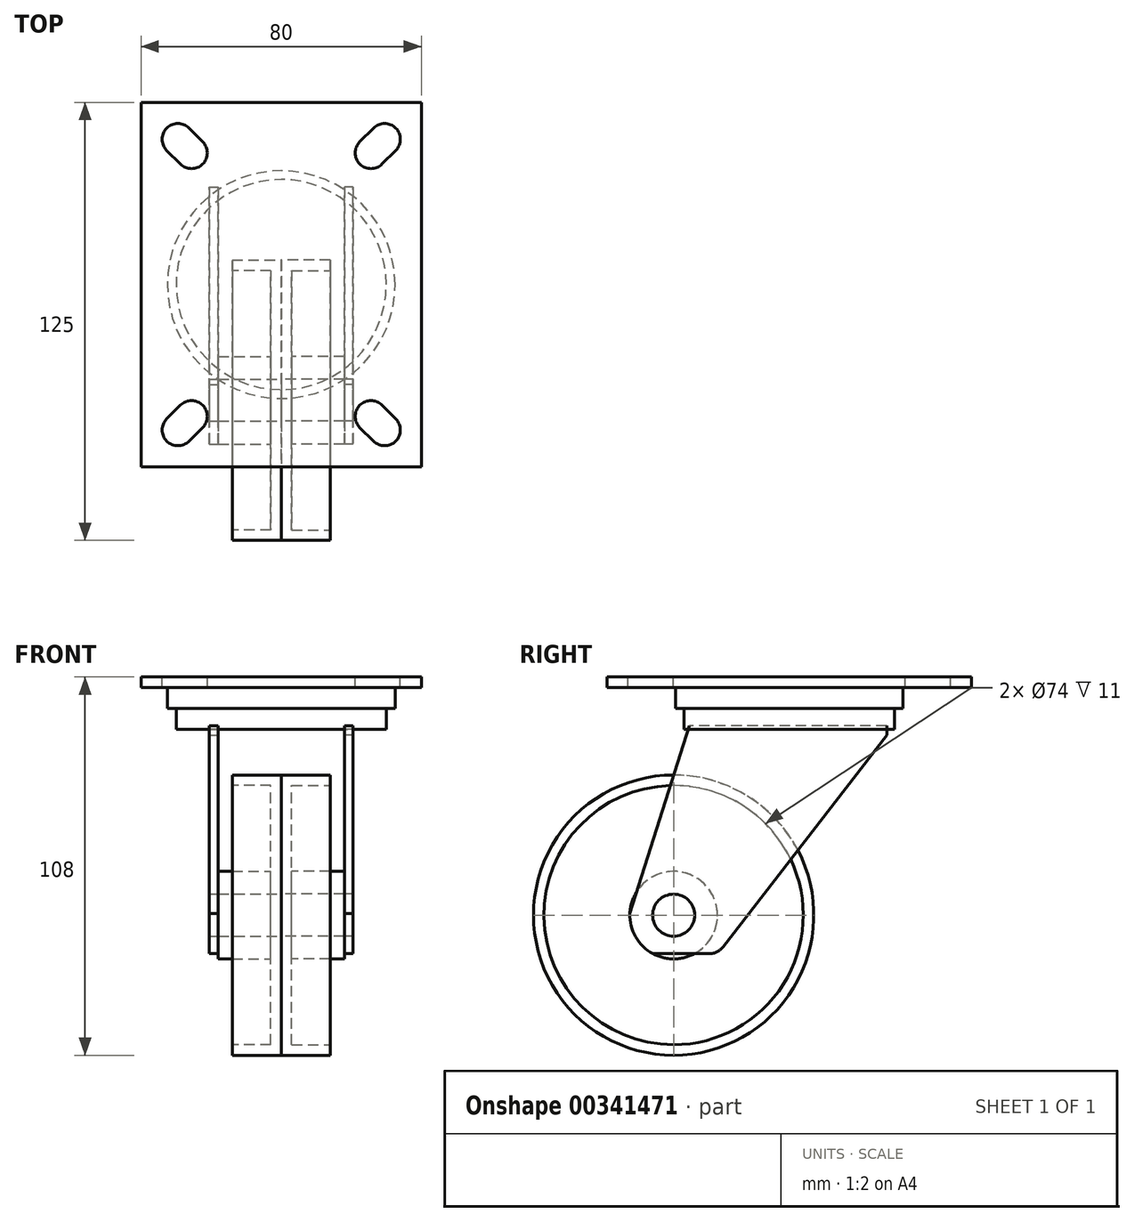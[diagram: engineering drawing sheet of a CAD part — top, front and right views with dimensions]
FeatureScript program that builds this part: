
annotation { "Feature Type Name" : "Feature", "Feature Type Description" : "" }
export const myFeature = defineFeature(function(context is Context, id is Id, definition is map)
    precondition{}
    {
        {
            var Q0;
            Q0=qCreatedBy(makeId("Front.planeOp"),FACE);
            var sketch = newSketch(context, id + "F0", { "sketchPlane" : qUnion([Q0])});
            skLineSegment(sketch, "E0.bottom", {"start": v(-49.77, 0) * mm, "end": v(53.7, 0) * mm, "construction": true});
            skLineSegment(sketch, "E0.top", {"start": v(-49.77, -108) * mm, "end": v(53.7, -108) * mm, "construction": true});
            skLineSegment(sketch, "E0.left", {"start": v(-49.77, 0) * mm, "end": v(-49.77, -108) * mm, "construction": true});
            skLineSegment(sketch, "E0.right", {"start": v(53.7, 0) * mm, "end": v(53.7, -108) * mm, "construction": true});
            skSolve(sketch);
        }
        {
            var Q0;
            Q0=qCreatedBy(makeId("Top.planeOp"),FACE);
            var sketch = newSketch(context, id + "F1", { "sketchPlane" : qUnion([Q0])});
            skLineSegment(sketch, "E1.bottom", {"start": v(-40, 52) * mm, "end": v(40, 52) * mm});
            skLineSegment(sketch, "E1.top", {"start": v(-40, -52) * mm, "end": v(40, -52) * mm});
            skLineSegment(sketch, "E1.left", {"start": v(-40, 52) * mm, "end": v(-40, -52) * mm});
            skLineSegment(sketch, "E1.right", {"start": v(40, 52) * mm, "end": v(40, -52) * mm});
            skLineSegment(sketch, "E2", {"start": v(0, 52) * mm, "end": v(0, -52) * mm, "construction": true});
            skLineSegment(sketch, "E3", {"start": v(-40, 0) * mm, "end": v(0, 0) * mm, "construction": true});
            skLineSegment(sketch, "E4", {"start": v(0, 0) * mm, "end": v(40, 0) * mm, "construction": true});
            skArc(sketch, "E5", {"start": v(-26.32, 44.68) * mm, "mid": v(-32.68, 44.68) * mm, "end": v(-32.68, 38.32) * mm});
            skLineSegment(sketch, "E6", {"start": v(-29.5, 41.5) * mm, "end": v(-26.32, 44.68) * mm, "construction": true});
            skLineSegment(sketch, "E7", {"start": v(-26.32, 44.68) * mm, "end": v(-22.43, 40.8) * mm});
            skLineSegment(sketch, "E8", {"start": v(-22.43, 40.8) * mm, "end": v(-28.8, 34.43) * mm, "construction": true});
            skLineSegment(sketch, "E9", {"start": v(-28.8, 34.43) * mm, "end": v(-32.68, 38.32) * mm});
            skLineSegment(sketch, "E10", {"start": v(-32.68, 38.32) * mm, "end": v(-29.5, 41.5) * mm, "construction": true});
            skLineSegment(sketch, "E11", {"start": v(-29.5, 41.5) * mm, "end": v(-25, 41.5) * mm, "construction": true});
            skArc(sketch, "E12", {"start": v(-28.8, 34.43) * mm, "mid": v(-22.43, 34.43) * mm, "end": v(-22.43, 40.8) * mm});
            skLineSegment(sketch, "E13.MirrorCS", {"start": v(28.8, 34.43) * mm, "end": v(32.68, 38.32) * mm});
            skArc(sketch, "E14.MirrorCS", {"start": v(26.32, 44.68) * mm, "mid": v(32.68, 44.68) * mm, "end": v(32.68, 38.32) * mm});
            skLineSegment(sketch, "E15.MirrorCS", {"start": v(26.32, 44.68) * mm, "end": v(22.43, 40.8) * mm});
            skArc(sketch, "E16.MirrorCS", {"start": v(28.8, 34.43) * mm, "mid": v(22.43, 34.43) * mm, "end": v(22.43, 40.8) * mm});
            skLineSegment(sketch, "E17.MirrorCS", {"start": v(-28.8, -34.43) * mm, "end": v(-32.68, -38.32) * mm});
            skArc(sketch, "E18.MirrorCS", {"start": v(-28.8, -34.43) * mm, "mid": v(-22.43, -34.43) * mm, "end": v(-22.43, -40.8) * mm});
            skLineSegment(sketch, "E19.MirrorCS", {"start": v(-26.32, -44.68) * mm, "end": v(-22.43, -40.8) * mm});
            skArc(sketch, "E20.MirrorCS", {"start": v(-26.32, -44.68) * mm, "mid": v(-32.68, -44.68) * mm, "end": v(-32.68, -38.32) * mm});
            skArc(sketch, "E21.MirrorCS", {"start": v(26.32, -44.68) * mm, "mid": v(32.68, -44.68) * mm, "end": v(32.68, -38.32) * mm});
            skArc(sketch, "E22.MirrorCS", {"start": v(28.8, -34.43) * mm, "mid": v(22.43, -34.43) * mm, "end": v(22.43, -40.8) * mm});
            skLineSegment(sketch, "E23.MirrorCS", {"start": v(26.32, -44.68) * mm, "end": v(22.43, -40.8) * mm});
            skLineSegment(sketch, "E24.MirrorCS", {"start": v(28.8, -34.43) * mm, "end": v(32.68, -38.32) * mm});
            skLineSegment(sketch, "E25", {"start": v(24.37, -42.74) * mm, "end": v(30.74, -36.37) * mm, "construction": true});
            skLineSegment(sketch, "E26", {"start": v(27.56, -39.56) * mm, "end": v(0, -39.56) * mm, "construction": true});
            skLineSegment(sketch, "E27", {"start": v(27.56, -39.56) * mm, "end": v(27.56, 0) * mm, "construction": true});
            skSolve(sketch);
        }
        {
            var Q0;
            Q0=makeQuery(id+"F1.imprint","IMPRINT",FACE,{"disambiguationData":[TD([[makeQuery(id+"F1.imprint","IMPRINT",EDGE,{"derivedFrom":sQuery(id+"F1.wireOp",EDGE,"E1.bottom")}),-1.0]])]});
            extrude(context, id + "F2", {"entities" : qUnion([Q0]), "oppositeDirection" : true, "depth" : 3 * mm});
        }
        {
            var Q0;
            Q0=qCreatedBy(makeId("Right.planeOp"),FACE);
            var sketch = newSketch(context, id + "F3", { "sketchPlane" : qUnion([Q0])});
            skCircle(sketch, "E28", {"center": v(-33, -68) * mm, "radius": 40 * mm});
            skLineSegment(sketch, "E29", {"start": v(17.4, -108) * mm, "end": v(-52.03, -108) * mm, "construction": true});
            skCircle(sketch, "E30", {"center": v(-33, -68) * mm, "radius": 6 * mm});
            skCircle(sketch, "E31", {"center": v(-33, -68) * mm, "radius": 12.5 * mm});
            skSolve(sketch);
        }
        {
            var Q0;
            Q0=makeQuery(id+"F3.imprint","IMPRINT",FACE,{"disambiguationData":[TD([[makeQuery(id+"F3.imprint","IMPRINT",EDGE,{"derivedFrom":sQuery(id+"F3.wireOp",EDGE,"E28")}),1.0]])]});
            extrude(context, id + "F4", {"entities" : qUnion([Q0]), "depth" : 28 / 2 * mm});
        }
        {
            var Q0;
            Q0=makeQuery(id+"F4.opExtrude","CAP_FACE",FACE,{"disambiguationData":[OSD([sQuery(id+"F3.wireOp",EDGE,"E28")])],"isStart":false});
            var sketch = newSketch(context, id + "F5", { "sketchPlane" : qUnion([Q0])});
            skCircle(sketch, "E32", {"center": v(-33, -68) * mm, "radius": 37 * mm});
            skSolve(sketch);
        }
        {
            var Q0;
            Q0=makeQuery(id+"F5.imprint","IMPRINT",FACE,{"disambiguationData":[TD([[makeQuery(id+"F5.imprint","IMPRINT",EDGE,{"derivedFrom":sQuery(id+"F5.wireOp",EDGE,"E32")}),1.0]])]});
            extrude(context, id + "F6", {"entities" : qUnion([Q0]), "operationType" : NewBodyOperationType.REMOVE, "oppositeDirection" : true, "depth" : (28 / 2 - 3) * mm});
        }
        {
            var Q0;
            Q0=makeQuery(id+"F3.imprint","IMPRINT",FACE,{"disambiguationData":[TD([[makeQuery(id+"F3.imprint","IMPRINT",EDGE,{"derivedFrom":sQuery(id+"F3.wireOp",EDGE,"E30")}),-1.0]])]});
            extrude(context, id + "F7", {"entities" : qUnion([Q0]), "operationType" : NewBodyOperationType.ADD, "depth" : 36 / 2 * mm});
        }
        {
            var Q0;
            Q0=makeQuery(id+"F4.opExtrude","SWEPT_BODY",BODY,{"disambiguationData":[OSD([sQuery(id+"F3.wireOp",EDGE,"E28")])]});
            var Q1;
            Q1=qCreatedBy(makeId("Right.planeOp"),FACE);
            mirror(context, id + "F8", {"operationType" : NewBodyOperationType.ADD, "entities" : qUnion([Q0]), "mirrorPlane" : qUnion([Q1])});
        }
        {
            var Q0;
            Q0=makeQuery(id+"F2.opExtrude","CAP_FACE",FACE,{"disambiguationData":[OSD([sQuery(id+"F1.wireOp",EDGE,"E1.bottom"),sQuery(id+"F1.wireOp",EDGE,"E1.top"),sQuery(id+"F1.wireOp",EDGE,"E1.left"),sQuery(id+"F1.wireOp",EDGE,"E1.right"),sQuery(id+"F1.wireOp",EDGE,"E5"),sQuery(id+"F1.wireOp",EDGE,"RUgz7CMT-Dv4A-K8fF-msUp-G3Q1L3aIyYa7"),sQuery(id+"F1.wireOp",EDGE,"vzA3B5fi-1odL-VSCK-aFdr-y0MmKfKFnjQ4"),sQuery(id+"F1.wireOp",EDGE,"ONqdk7Bx-5njC-edYK-hXDO-9Puxu0bpny2q")])],"isStart":false});
            var sketch = newSketch(context, id + "F9", { "sketchPlane" : qUnion([Q0])});
            skCircle(sketch, "E33", {"center": v(0, 0) * mm, "radius": 32.5 * mm});
            skSolve(sketch);
        }
        {
            var Q0;
            Q0=makeQuery(id+"F9.imprint","IMPRINT",FACE,{"disambiguationData":[TD([[makeQuery(id+"F9.imprint","IMPRINT",EDGE,{"derivedFrom":sQuery(id+"F9.wireOp",EDGE,"E33")}),1.0]])]});
            extrude(context, id + "F10", {"entities" : qUnion([Q0]), "operationType" : NewBodyOperationType.ADD, "depth" : 6 * mm});
        }
        {
            var Q0;
            Q0=makeQuery(id+"F7.opExtrude","CAP_FACE",FACE,{"disambiguationData":[OSD([sQuery(id+"F3.wireOp",EDGE,"E30"),sQuery(id+"F3.wireOp",EDGE,"E31")])],"isStart":false});
            var sketch = newSketch(context, id + "F11", { "sketchPlane" : qUnion([Q0])});
            skCircle(sketch, "E34", {"center": v(-33, -68) * mm, "radius": 6 * mm});
            skLineSegment(sketch, "E35", {"start": v(-42.3, -79) * mm, "end": v(-22.86, -79) * mm});
            skLineSegment(sketch, "E36", {"start": v(-18.9, -77.06) * mm, "end": v(27.83, -16.55) * mm});
            skLineSegment(sketch, "E37", {"start": v(27.83, -16.55) * mm, "end": v(27.83, -13.95) * mm});
            skLineSegment(sketch, "E38", {"start": v(27.83, -13.95) * mm, "end": v(-28.55, -13.95) * mm});
            skLineSegment(sketch, "E39", {"start": v(-28.55, -13.95) * mm, "end": v(-47.06, -72.5) * mm});
            skPoint(sketch, "E40.visualSharp", {"position": v(-49.12, -79) * mm});
            skArc(sketch, "E40.filletArc", {"start": v(-47.06, -72.5) * mm, "mid": v(-46.33, -76.96) * mm, "end": v(-42.3, -79) * mm});
            skPoint(sketch, "E41.visualSharp", {"position": v(-20.4, -79) * mm});
            skArc(sketch, "E41.filletArc", {"start": v(-22.86, -79) * mm, "mid": v(-20.65, -78.49) * mm, "end": v(-18.9, -77.06) * mm});
            skSolve(sketch);
        }
        {
            var Q0;
            Q0=makeQuery(id+"F11.imprint","IMPRINT",FACE,{"disambiguationData":[TD([[makeQuery(id+"F11.imprint","IMPRINT",EDGE,{"derivedFrom":sQuery(id+"F11.wireOp",EDGE,"E36")}),1.0]])]});
            var Q1;
            Q1=makeQuery(id+"F11.imprint","IMPRINT",FACE,{"disambiguationData":[TD([[makeQuery(id+"F11.imprint","IMPRINT",EDGE,{"derivedFrom":sQuery(id+"F11.wireOp",EDGE,"E34")}),-1.0]])]});
            extrude(context, id + "F12", {"entities" : qUnion([Q0, Q1]), "depth" : 2.5 * mm});
        }
        {
            var Q0;
            Q0=makeQuery(id+"F12.opExtrude","SWEPT_BODY",BODY,{"disambiguationData":[OSD([sQuery(id+"F3.wireOp",EDGE,"E31"),sQuery(id+"F11.wireOp",EDGE,"E34"),sQuery(id+"F11.wireOp",EDGE,"E35"),sQuery(id+"F11.wireOp",EDGE,"E36"),sQuery(id+"F11.wireOp",EDGE,"E37"),sQuery(id+"F11.wireOp",EDGE,"E38"),sQuery(id+"F11.wireOp",EDGE,"E39"),sQuery(id+"F11.wireOp",EDGE,"E41.filletArc")])]});
            var Q1;
            Q1=qCreatedBy(makeId("Right.planeOp"),FACE);
            mirror(context, id + "F13", {"entities" : qUnion([Q0]), "mirrorPlane" : qUnion([Q1])});
        }
        {
            var Q0;
            Q0=makeQuery(id+"F10.opExtrude","CAP_FACE",FACE,{"disambiguationData":[OSD([sQuery(id+"F9.wireOp",EDGE,"E33")])],"isStart":false});
            var sketch = newSketch(context, id + "F14", { "sketchPlane" : qUnion([Q0])});
            skCircle(sketch, "E42", {"center": v(0, 0) * mm, "radius": 30 * mm});
            skSolve(sketch);
        }
        {
            var Q0;
            Q0=makeQuery(id+"F14.imprint","IMPRINT",FACE,{"disambiguationData":[TD([[makeQuery(id+"F14.imprint","IMPRINT",EDGE,{"derivedFrom":sQuery(id+"F14.wireOp",EDGE,"E42")}),1.0]])]});
            extrude(context, id + "F15", {"entities" : qUnion([Q0]), "depth" : 6 * mm});
        }
    });
